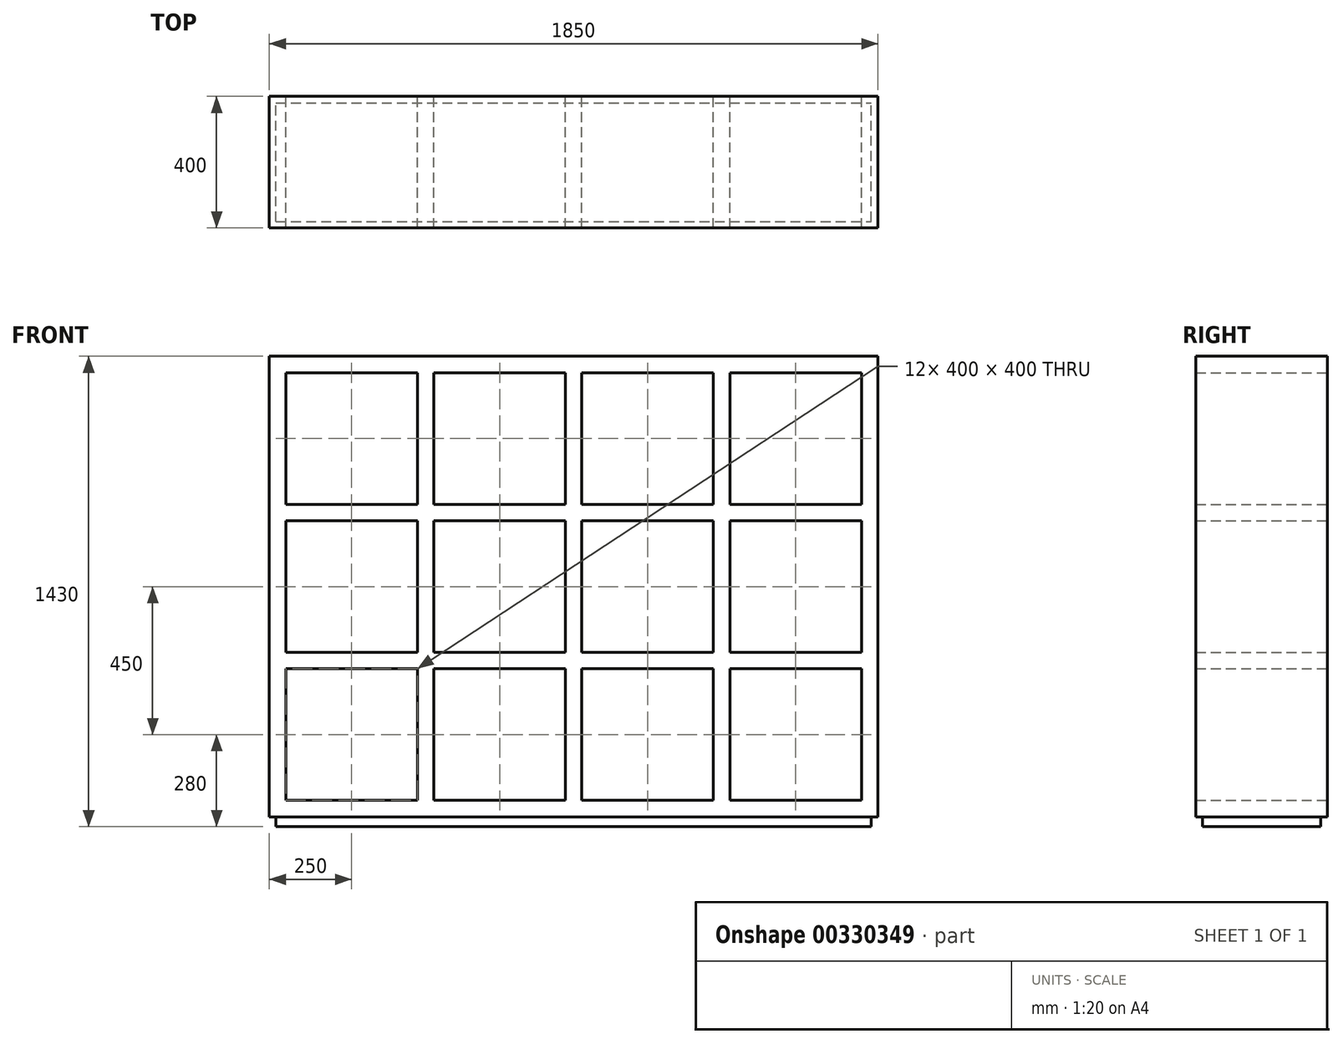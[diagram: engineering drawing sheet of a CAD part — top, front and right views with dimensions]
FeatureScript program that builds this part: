
annotation { "Feature Type Name" : "Feature", "Feature Type Description" : "" }
export const myFeature = defineFeature(function(context is Context, id is Id, definition is map)
    precondition{}
    {
        {
            var Q0;
            Q0=qCreatedBy(makeId("Front.planeOp"),FACE);
            var sketch = newSketch(context, id + "F0", { "sketchPlane" : qUnion([Q0])});
            skLineSegment(sketch, "E0.bottom", {"start": v(0, 0) * mm, "end": v(1850, 0) * mm});
            skLineSegment(sketch, "E0.top", {"start": v(0, 1400) * mm, "end": v(1850, 1400) * mm});
            skLineSegment(sketch, "E0.left", {"start": v(0, 0) * mm, "end": v(0, 1400) * mm});
            skLineSegment(sketch, "E0.right", {"start": v(1850, 0) * mm, "end": v(1850, 1400) * mm});
            skLineSegment(sketch, "E1.bottom", {"start": v(50, 50) * mm, "end": v(450, 50) * mm});
            skLineSegment(sketch, "E1.top", {"start": v(50, 450) * mm, "end": v(450, 450) * mm});
            skLineSegment(sketch, "E1.left", {"start": v(50, 50) * mm, "end": v(50, 450) * mm});
            skLineSegment(sketch, "E1.right", {"start": v(450, 50) * mm, "end": v(450, 450) * mm});
            skLineSegment(sketch, "E2.0.1.0", {"start": v(50, 900) * mm, "end": v(450, 900) * mm});
            skLineSegment(sketch, "E2.0.1.1", {"start": v(50, 500) * mm, "end": v(50, 900) * mm});
            skLineSegment(sketch, "E2.0.1.2", {"start": v(50, 500) * mm, "end": v(450, 500) * mm});
            skLineSegment(sketch, "E2.0.1.3", {"start": v(450, 500) * mm, "end": v(450, 900) * mm});
            skLineSegment(sketch, "E2.0.2.0", {"start": v(50, 1350) * mm, "end": v(450, 1350) * mm});
            skLineSegment(sketch, "E2.0.2.1", {"start": v(50, 950) * mm, "end": v(50, 1350) * mm});
            skLineSegment(sketch, "E2.0.2.2", {"start": v(50, 950) * mm, "end": v(450, 950) * mm});
            skLineSegment(sketch, "E2.0.2.3", {"start": v(450, 950) * mm, "end": v(450, 1350) * mm});
            skLineSegment(sketch, "E2.1.0.0", {"start": v(500, 450) * mm, "end": v(900, 450) * mm});
            skLineSegment(sketch, "E2.1.0.1", {"start": v(500, 50) * mm, "end": v(500, 450) * mm});
            skLineSegment(sketch, "E2.1.0.2", {"start": v(500, 50) * mm, "end": v(900, 50) * mm});
            skLineSegment(sketch, "E2.1.0.3", {"start": v(900, 50) * mm, "end": v(900, 450) * mm});
            skLineSegment(sketch, "E2.1.1.0", {"start": v(500, 900) * mm, "end": v(900, 900) * mm});
            skLineSegment(sketch, "E2.1.1.1", {"start": v(500, 500) * mm, "end": v(500, 900) * mm});
            skLineSegment(sketch, "E2.1.1.2", {"start": v(500, 500) * mm, "end": v(900, 500) * mm});
            skLineSegment(sketch, "E2.1.1.3", {"start": v(900, 500) * mm, "end": v(900, 900) * mm});
            skLineSegment(sketch, "E2.1.2.0", {"start": v(500, 1350) * mm, "end": v(900, 1350) * mm});
            skLineSegment(sketch, "E2.1.2.1", {"start": v(500, 950) * mm, "end": v(500, 1350) * mm});
            skLineSegment(sketch, "E2.1.2.2", {"start": v(500, 950) * mm, "end": v(900, 950) * mm});
            skLineSegment(sketch, "E2.1.2.3", {"start": v(900, 950) * mm, "end": v(900, 1350) * mm});
            skLineSegment(sketch, "E2.2.0.0", {"start": v(950, 450) * mm, "end": v(1350, 450) * mm});
            skLineSegment(sketch, "E2.2.0.1", {"start": v(950, 50) * mm, "end": v(950, 450) * mm});
            skLineSegment(sketch, "E2.2.0.2", {"start": v(950, 50) * mm, "end": v(1350, 50) * mm});
            skLineSegment(sketch, "E2.2.0.3", {"start": v(1350, 50) * mm, "end": v(1350, 450) * mm});
            skLineSegment(sketch, "E2.2.1.0", {"start": v(950, 900) * mm, "end": v(1350, 900) * mm});
            skLineSegment(sketch, "E2.2.1.1", {"start": v(950, 500) * mm, "end": v(950, 900) * mm});
            skLineSegment(sketch, "E2.2.1.2", {"start": v(950, 500) * mm, "end": v(1350, 500) * mm});
            skLineSegment(sketch, "E2.2.1.3", {"start": v(1350, 500) * mm, "end": v(1350, 900) * mm});
            skLineSegment(sketch, "E2.2.2.0", {"start": v(950, 1350) * mm, "end": v(1350, 1350) * mm});
            skLineSegment(sketch, "E2.2.2.1", {"start": v(950, 950) * mm, "end": v(950, 1350) * mm});
            skLineSegment(sketch, "E2.2.2.2", {"start": v(950, 950) * mm, "end": v(1350, 950) * mm});
            skLineSegment(sketch, "E2.2.2.3", {"start": v(1350, 950) * mm, "end": v(1350, 1350) * mm});
            skLineSegment(sketch, "E2.3.0.0", {"start": v(1400, 450) * mm, "end": v(1800, 450) * mm});
            skLineSegment(sketch, "E2.3.0.1", {"start": v(1400, 50) * mm, "end": v(1400, 450) * mm});
            skLineSegment(sketch, "E2.3.0.2", {"start": v(1400, 50) * mm, "end": v(1800, 50) * mm});
            skLineSegment(sketch, "E2.3.0.3", {"start": v(1800, 50) * mm, "end": v(1800, 450) * mm});
            skLineSegment(sketch, "E2.3.1.0", {"start": v(1400, 900) * mm, "end": v(1800, 900) * mm});
            skLineSegment(sketch, "E2.3.1.1", {"start": v(1400, 500) * mm, "end": v(1400, 900) * mm});
            skLineSegment(sketch, "E2.3.1.2", {"start": v(1400, 500) * mm, "end": v(1800, 500) * mm});
            skLineSegment(sketch, "E2.3.1.3", {"start": v(1800, 500) * mm, "end": v(1800, 900) * mm});
            skLineSegment(sketch, "E2.3.2.0", {"start": v(1400, 1350) * mm, "end": v(1800, 1350) * mm});
            skLineSegment(sketch, "E2.3.2.1", {"start": v(1400, 950) * mm, "end": v(1400, 1350) * mm});
            skLineSegment(sketch, "E2.3.2.2", {"start": v(1400, 950) * mm, "end": v(1800, 950) * mm});
            skLineSegment(sketch, "E2.3.2.3", {"start": v(1800, 950) * mm, "end": v(1800, 1350) * mm});
            skLineSegment(sketch, "E2.direction1", {"start": v(50, 50) * mm, "end": v(500, 50) * mm, "construction": true});
            skLineSegment(sketch, "E2.direction2", {"start": v(50, 50) * mm, "end": v(50, 500) * mm, "construction": true});
            skSolve(sketch);
        }
        {
            var Q0;
            Q0 = qSketchRegion(id + "F0", true);
            extrude(context, id + "F1", {"entities" : qUnion([Q0]), "depth" : 400 * mm});
        }
        {
            var Q0;
            Q0=makeQuery(id+"F1.opExtrude","SWEPT_FACE",FACE,{"disambiguationData":[OSD([sQuery(id+"F0.wireOp",EDGE,"E0.bottom")])]});
            var sketch = newSketch(context, id + "F2", { "sketchPlane" : qUnion([Q0])});
            skLineSegment(sketch, "E3.bottom", {"start": v(20, 380) * mm, "end": v(1830, 380) * mm});
            skLineSegment(sketch, "E3.top", {"start": v(20, 20) * mm, "end": v(1830, 20) * mm});
            skLineSegment(sketch, "E3.left", {"start": v(20, 380) * mm, "end": v(20, 20) * mm});
            skLineSegment(sketch, "E3.right", {"start": v(1830, 380) * mm, "end": v(1830, 20) * mm});
            skSolve(sketch);
        }
        {
            var Q0;
            Q0 = qSketchRegion(id + "F2", true);
            extrude(context, id + "F3", {"entities" : qUnion([Q0]), "operationType" : NewBodyOperationType.ADD, "depth" : 30 * mm});
        }
    });
